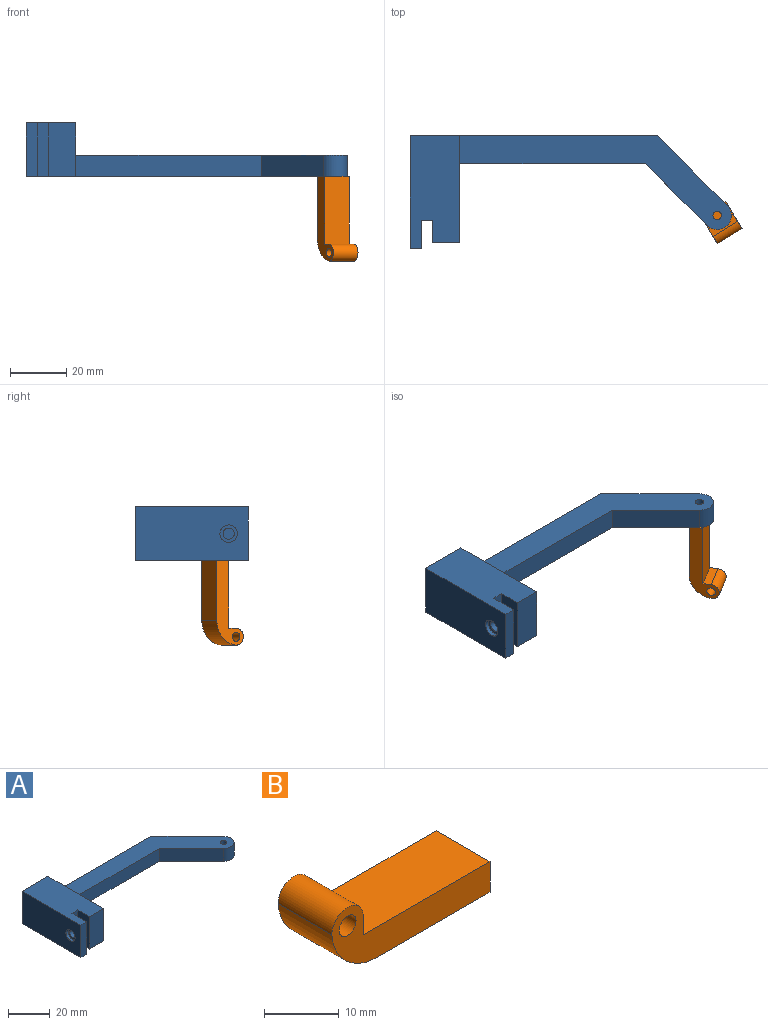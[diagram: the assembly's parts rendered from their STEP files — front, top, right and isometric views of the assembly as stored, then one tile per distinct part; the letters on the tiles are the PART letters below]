
ASSEMBLY  parts=2 mates=1
PART A: 19 faces, bbox 113.8x40x19 mm
  f0: plane 96.21x33.28mm, normal (0,0,1), area 1040.8mm2, adj f2,f13,f14,f15,f16,f17,f18
  f1: plane 113.81x40mm, normal (0,0,-1), area 1685.6mm2, adj f2,f3,f5,f6,f7,f8,f9,f13
  f2: plane 38x19mm, normal (1,0,0), area 647mm2, adj f0,f1,f4,f5,f13,f14
  f3: plane 19x8mm, normal (-1,0,0), area 152mm2, adj f1,f4,f5,f6
  f4: plane 40x17.6mm, normal (0,0,1), area 644.8mm2, adj f2,f3,f5,f6,f7,f8,f9,f13
  f5: plane 19x9.6mm, normal (0,-1,0), area 182.4mm2, adj f1,f2,f3,f4
  f6: plane 19x4mm, normal (0,-1,0), area 76mm2, adj f1,f3,f4,f8
  f7: plane 40x19mm, normal (-1,0,0), area 729.8mm2, adj f1,f4,f9,f11,f13
  f8: plane 19x10mm, normal (1,0,0), area 177.4mm2, adj f1,f4,f6,f9,f10
  f9: plane 19x4mm, normal (0,-1,0), area 76mm2, adj f1,f4,f7,f8
  f10: cylinder r=2mm len=4mm, axis (-1,0,0), area 31.4mm2, adj f8,f12
  f11: cylinder r=3.1mm len=6.2mm, axis (-1,0,0), area 29.2mm2, adj f7,f12
  f12: plane 6.2x6.2mm, normal (-1,0,0), area 17.6mm2, adj f10,f11
  f13: plane 87.6x19mm, normal (0,1,0), area 859.4mm2, adj f0,f1,f2,f4,f7,f15
  f14: plane 65.86x7.5mm, normal (0,-1,0), area 493.9mm2, adj f0,f1,f2,f17
  f15: plane 24.75x24.75mm, normal (0.71,0.71,0), area 262.5mm2, adj f0,f1,f13,f18
  f16: cylinder r=1.5mm len=7.5mm, axis (0,0,1), area 70.7mm2, adj f0,f1
  f17: plane 21.82x21.82mm, normal (-0.71,-0.71,0), area 231.4mm2, adj f0,f1,f14,f18
  f18: cylinder r=5mm len=8.54mm, axis (0,0,-1), area 117.8mm2, adj f0,f1,f15,f17
PART B: 11 faces, bbox 30x10.2x11 mm
  f0: plane 24x10.2mm, normal (0,0,1), area 244.8mm2, adj f1,f2,f3,f5
  f1: plane 30x11mm, normal (0,-1,0), area 158.1mm2, adj f0,f2,f4,f5,f6,f7,f8
  f2: plane 10.2x5mm, normal (1,0,0), area 43.9mm2, adj f0,f1,f3,f4,f9
  f3: plane 30x11mm, normal (0,1,0), area 158.1mm2, adj f0,f2,f4,f5,f6,f7,f8
  f4: plane 21.34x10.2mm, normal (0,0,-1), area 217.6mm2, adj f1,f2,f3,f8
  f5: plane 10.2x3mm, normal (1,0,0), area 30.6mm2, adj f0,f1,f3,f7
  f6: cylinder r=1.6mm len=10.2mm, axis (0,-1,0), area 102.5mm2, adj f1,f3
  f7: cylinder r=3mm len=10.2mm, axis (0,-1,0), area 96.1mm2, adj f1,f3,f5,f8
  f8: cylinder r=8.69mm len=10.2mm, axis (0,-1,0), area 132.2mm2, adj f1,f3,f4,f7
  f9: cylinder r=1.5mm len=7mm, axis (1,0,0), area 66mm2, adj f2,f10
  f10: plane 3x3mm, normal (1,0,0), area 7.1mm2, adj f9
PLACE A t=(-22,-0.41,10.75)mm fixed
PLACE B rot(axis=(0.66,-0.37,0.66),139.5deg) t=(72.71,3.44,-13.75)mm
MATE revolute A.f16 <-> B.f9  axis (0,0,-1) through (74.02,1.31,1.25)mm
